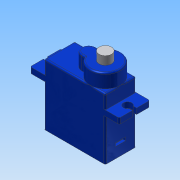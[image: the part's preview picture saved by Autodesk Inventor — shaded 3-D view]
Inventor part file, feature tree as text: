
AUTODESK INVENTOR PART (.ipt)
format: ipt  version: 2015 (Build 190159000, 159)  size: 250,880 bytes
history: native  units: mm
features: extrude x5, sketch x5, other x2, fillet x1
ambient origin geometry x8: Origin, YZ Plane, XZ Plane, XY Plane, X Axis, Y Axis, Z Axis, Center Point
bodies: Body1 (feature_tree)
feature tree (13):
  other  "솔리드1"
  extrude  "돌출1"  Depth=22.0mm
  other  "작업 평면1"
  extrude  "돌출2"  Depth=11.0mm
  extrude  "돌출3"  Depth=22.0mm TaperAngle=0.0deg
  fillet  "모깎기1"  [1 undecoded]
  extrude  "돌출4"  Depth=5.0mm
  extrude  "돌출6"  Depth=5.0mm
  sketch  "스케치1"
  sketch  "스케치2"
  sketch  "스케치3"
  sketch  "스케치4"
  sketch  "스케치6"
note: 1 required parameter value undecoded (feature->parameter linkage not recoverable at this tier; creation-order binding heuristic only, values carry confidence <= 0.55)
